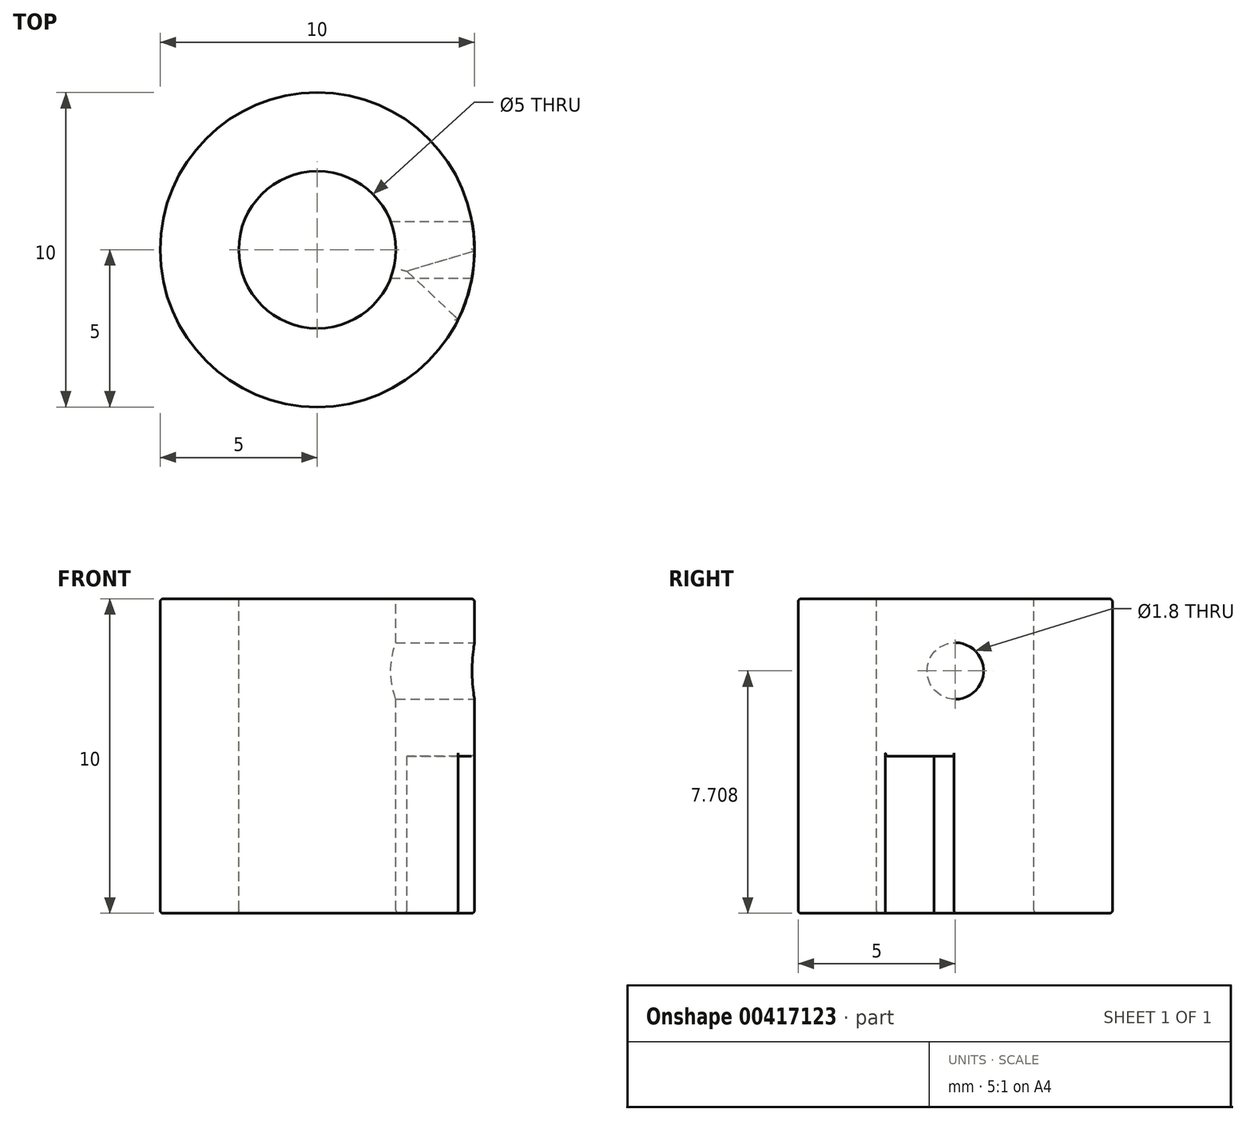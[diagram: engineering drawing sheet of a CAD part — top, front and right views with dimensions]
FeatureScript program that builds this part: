
annotation { "Feature Type Name" : "Feature", "Feature Type Description" : "" }
export const myFeature = defineFeature(function(context is Context, id is Id, definition is map)
    precondition{}
    {
        {
            var Q0;
            Q0=qCreatedBy(makeId("Top.planeOp"),FACE);
            var sketch = newSketch(context, id + "F0", { "sketchPlane" : qUnion([Q0])});
            skCircle(sketch, "E0", {"center": v(0, 0) * mm, "radius": 2.5 * mm});
            skCircle(sketch, "E1", {"center": v(0, 0) * mm, "radius": 5.25 * mm});
            skCircle(sketch, "E2", {"center": v(0, 0) * mm, "radius": 5 * mm});
            skSolve(sketch);
        }
        {
            var Q0;
            Q0=makeQuery(id+"F0.imprint","IMPRINT",FACE,{"disambiguationData":[TD([[makeQuery(id+"F0.imprint","IMPRINT",EDGE,{"derivedFrom":sQuery(id+"F0.wireOp",EDGE,"E0")}),-1.0]])]});
            extrude(context, id + "F1", {"entities" : qUnion([Q0]), "oppositeDirection" : true, "depth" : 5 * mm});
        }
        {
            var Q0;
            Q0=qCreatedBy(makeId("Top.planeOp"),FACE);
            var sketch = newSketch(context, id + "F2", { "sketchPlane" : qUnion([Q0])});
            skLineSegment(sketch, "E3", {"start": v(5.25, 0.03) * mm, "end": v(2.85, -0.68) * mm});
            skLineSegment(sketch, "E4", {"start": v(2.85, -0.68) * mm, "end": v(4.67, -2.4) * mm});
            skLineSegment(sketch, "E5", {"start": v(4.67, -2.4) * mm, "end": v(5.25, 0.03) * mm});
            skSolve(sketch);
        }
        {
            var Q0;
            Q0=makeQuery(id+"F2.imprint","IMPRINT",FACE,{"disambiguationData":[TD([[makeQuery(id+"F2.imprint","IMPRINT",EDGE,{"derivedFrom":sQuery(id+"F2.wireOp",EDGE,"E3")}),1.0]])]});
            extrude(context, id + "F3", {"entities" : qUnion([Q0]), "operationType" : NewBodyOperationType.REMOVE, "oppositeDirection" : true, "depth" : 5 * mm});
        }
        {
            var Q0;
            Q0=qCreatedBy(makeId("Right.planeOp"),FACE);
            var sketch = newSketch(context, id + "F4", { "sketchPlane" : qUnion([Q0])});
            skLineSegment(sketch, "E6", {"start": v(0, 10.22) * mm, "end": v(0, -17) * mm, "construction": true});
            skSolve(sketch);
        }
        {
            var Q0;
            Q0=makeQuery(id+"F0.imprint","IMPRINT",FACE,{"disambiguationData":[TD([[makeQuery(id+"F0.imprint","IMPRINT",EDGE,{"derivedFrom":sQuery(id+"F0.wireOp",EDGE,"E0")}),-1.0]])]});
            extrude(context, id + "F5", {"entities" : qUnion([Q0]), "operationType" : NewBodyOperationType.ADD, "depth" : 5 * mm});
        }
        {
            var Q0;
            Q0=qCreatedBy(makeId("Right.planeOp"),FACE);
            cPlane(context, id + "F6", {"entities" : qUnion([Q0]), "cplaneType" : CPlaneType.OFFSET, "offset" : 5 * mm, "width" : 150 * mm, "height" : 150 * mm});
        }
        {
            var Q0;
            Q0=qCreatedBy(id+"F6.planeOp",FACE);
            var sketch = newSketch(context, id + "F7", { "sketchPlane" : qUnion([Q0])});
            skPoint(sketch, "E7", {"position": v(0, 2.7) * mm});
            skSolve(sketch);
        }
        {
            var Q0;
            Q0=sQuery(id+"F7.wireOp",VERTEX,"E7");
            var Q1;
            Q1=makeQuery(id+"F1.opExtrude","SWEPT_BODY",BODY,{"disambiguationData":[OSD([sQuery(id+"F0.wireOp",EDGE,"E0"),sQuery(id+"F0.wireOp",EDGE,"E2")])]});
            hole(context, id + "F8", {"style" : HoleStyle.SIMPLE, "endStyle" : HoleEndStyle.BLIND, "holeDiameter" : 1.8 * mm, "holeDepth" : 3 * mm, "isTappedThrough" : true, "tappedDepth" : 12 * mm, "tapClearance" : 3, "locations" : qUnion([Q0]), "scope" : qUnion([Q1])});
        }
        {
            var Q0;
            Q0=makeQuery(id+"F1.opExtrude","CAP_FACE",FACE,{"disambiguationData":[OSD([sQuery(id+"F0.wireOp",EDGE,"E0"),sQuery(id+"F0.wireOp",EDGE,"E2")])],"isStart":false});
            fillet(context, id + "F9", {"entities" : qUnion([Q0]), "radius" : .1 * mm, "tangentPropagation" : true, "allowEdgeOverflow" : false});
        }
        {
            var Q0;
            Q0=makeQuery(id+"F5.opExtrude","CAP_EDGE",EDGE,{"disambiguationData":[OSD([sQuery(id+"F0.wireOp",EDGE,"E2")])],"isStart":true});
            var Q1;
            Q1=makeQuery(id+"F5.opExtrude","CAP_EDGE",EDGE,{"disambiguationData":[OSD([sQuery(id+"F0.wireOp",EDGE,"E2")])],"isStart":false});
            fillet(context, id + "F10", {"entities" : qUnion([Q0, Q1]), "radius" : .1 * mm, "tangentPropagation" : true, "allowEdgeOverflow" : false});
        }
    });
